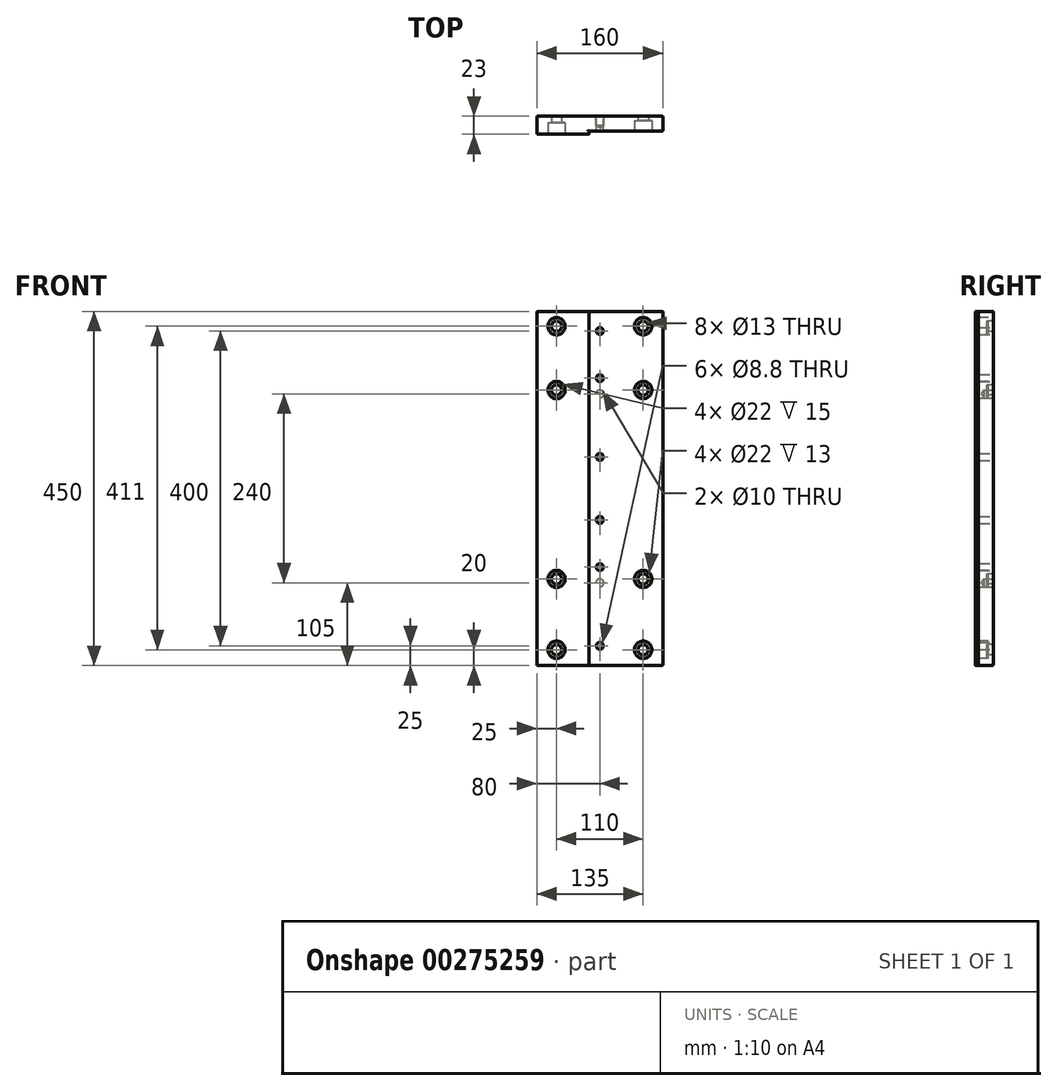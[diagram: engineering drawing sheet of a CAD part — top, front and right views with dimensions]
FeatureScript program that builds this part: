
annotation { "Feature Type Name" : "Feature", "Feature Type Description" : "" }
export const myFeature = defineFeature(function(context is Context, id is Id, definition is map)
    precondition{}
    {
        {
            var Q0;
            Q0=qCreatedBy(makeId("Front.planeOp"),FACE);
            var sketch = newSketch(context, id + "F0", { "sketchPlane" : qUnion([Q0])});
            skLineSegment(sketch, "E0.bottom", {"start": v(80, -225) * mm, "end": v(-80, -225) * mm});
            skLineSegment(sketch, "E0.top", {"start": v(80, 225) * mm, "end": v(-80, 225) * mm});
            skLineSegment(sketch, "E0.left", {"start": v(80, -225) * mm, "end": v(80, 225) * mm});
            skLineSegment(sketch, "E0.right", {"start": v(-80, -225) * mm, "end": v(-80, 225) * mm});
            skPoint(sketch, "E0.middle", {"position": v(0, 0) * mm});
            skLineSegment(sketch, "E1", {"start": v(0, 280.93) * mm, "end": v(0, -292.93) * mm, "construction": true});
            skLineSegment(sketch, "E2", {"start": v(-14, 225) * mm, "end": v(-14, -225) * mm});
            skLineSegment(sketch, "E3", {"start": v(-59.7, 206) * mm, "end": v(63.96, 206) * mm, "construction": true});
            skLineSegment(sketch, "E4", {"start": v(-66.2, -205) * mm, "end": v(62.1, -205) * mm, "construction": true});
            skLineSegment(sketch, "E5", {"start": v(-55, 125) * mm, "end": v(57.45, 125) * mm, "construction": true});
            skLineSegment(sketch, "E6", {"start": v(-48.54, -115) * mm, "end": v(63.03, -115) * mm, "construction": true});
            skPoint(sketch, "E7", {"position": v(0, 200) * mm});
            skPoint(sketch, "E8", {"position": v(0, 140) * mm});
            skPoint(sketch, "E9", {"position": v(0, 120) * mm});
            skPoint(sketch, "E10", {"position": v(0, 40) * mm});
            skPoint(sketch, "E11", {"position": v(0, -40) * mm});
            skPoint(sketch, "E12", {"position": v(0, -100) * mm});
            skPoint(sketch, "E13", {"position": v(0, -120) * mm});
            skPoint(sketch, "E14", {"position": v(0, -200) * mm});
            skPoint(sketch, "E15", {"position": v(-55, 206) * mm});
            skPoint(sketch, "E16", {"position": v(55, 206) * mm});
            skPoint(sketch, "E17", {"position": v(-55, 125) * mm});
            skPoint(sketch, "E18", {"position": v(55, 125) * mm});
            skPoint(sketch, "E19", {"position": v(-55, -115) * mm});
            skPoint(sketch, "E20", {"position": v(55, -115) * mm});
            skPoint(sketch, "E21", {"position": v(-55, -205) * mm});
            skPoint(sketch, "E22", {"position": v(55, -205) * mm});
            skLineSegment(sketch, "E23", {"start": v(-55, -220.48) * mm, "end": v(-55, 225) * mm, "construction": true});
            skLineSegment(sketch, "E24.MirrorCS", {"start": v(55, -220.48) * mm, "end": v(55, 225) * mm, "construction": true});
            skSolve(sketch);
        }
        {
            var Q0;
            {var subQ0=sQuery(id+"F0.wireOp",EDGE,"E0.right");Q0=makeQuery(id+"F0.imprint","IMPRINT",FACE,{"disambiguationData":[TD([[makeQuery(id+"F0.imprint","IMPRINT",EDGE,{"derivedFrom":subQ0}),-1.0]])]});}
            extrude(context, id + "F1", {"entities" : qUnion([Q0]), "depth" : 23 * mm});
        }
        {
            var Q0;
            {var subQ0=sQuery(id+"F0.wireOp",EDGE,"E0.left");Q0=makeQuery(id+"F0.imprint","IMPRINT",FACE,{"disambiguationData":[TD([[makeQuery(id+"F0.imprint","IMPRINT",EDGE,{"derivedFrom":subQ0}),1.0]])]});}
            extrude(context, id + "F2", {"entities" : qUnion([Q0]), "operationType" : NewBodyOperationType.ADD, "depth" : 19 * mm});
        }
        {
            var Q0;
            Q0=sQuery(id+"F0.wireOp",VERTEX,"E13");
            var Q1;
            Q1=sQuery(id+"F0.wireOp",VERTEX,"E9");
            var Q2;
            Q2=makeQuery(id+"F1.opExtrude","SWEPT_BODY",BODY,{"disambiguationData":[OSD([sQuery(id+"F0.wireOp",EDGE,"E0.bottom"),sQuery(id+"F0.wireOp",EDGE,"E0.top"),sQuery(id+"F0.wireOp",EDGE,"E0.right"),sQuery(id+"F0.wireOp",EDGE,"E2")])]});
            hole(context, id + "F3", {"style" : HoleStyle.SIMPLE, "endStyle" : HoleEndStyle.BLIND, "oppositeDirection" : true, "holeDiameter" : 10 * mm, "holeDepth" : 12 * mm, "tappedDepth" : 12 * mm, "tapClearance" : 3, "startFromSketch" : true, "locations" : qUnion([Q0, Q1]), "scope" : qUnion([Q2])});
        }
        {
            var Q0;
            Q0=sQuery(id+"F0.wireOp",VERTEX,"E14");
            var Q1;
            Q1=sQuery(id+"F0.wireOp",VERTEX,"E12");
            var Q2;
            Q2=sQuery(id+"F0.wireOp",VERTEX,"E11");
            var Q3;
            Q3=sQuery(id+"F0.wireOp",VERTEX,"E10");
            var Q4;
            Q4=sQuery(id+"F0.wireOp",VERTEX,"E8");
            var Q5;
            Q5=sQuery(id+"F0.wireOp",VERTEX,"E7");
            var Q6;
            Q6=makeQuery(id+"F1.opExtrude","SWEPT_BODY",BODY,{"disambiguationData":[OSD([sQuery(id+"F0.wireOp",EDGE,"E0.bottom"),sQuery(id+"F0.wireOp",EDGE,"E0.top"),sQuery(id+"F0.wireOp",EDGE,"E0.right"),sQuery(id+"F0.wireOp",EDGE,"E2")])]});
            hole(context, id + "F4", {"style" : HoleStyle.SIMPLE, "endStyle" : HoleEndStyle.BLIND, "oppositeDirection" : true, "standardTappedOrClearance" : lookupTablePath({ "standard" : "ISO", "fit" : "Normal", "size" : "M8", "type" : "Clearance" }), "standardBlindInLast" : lookupTablePath({ "fit" : "Standard", "standard" : "ISO", "size" : "M8", "type" : "Clearance" }), "holeDiameter" : 8.8 * mm, "holeDepth" : 33 * mm, "tappedDepth" : 12 * mm, "tapClearance" : 3, "startFromSketch" : true, "locations" : qUnion([Q0, Q1, Q2, Q3, Q4, Q5]), "scope" : qUnion([Q6])});
        }
        {
            var Q0;
            Q0=makeQuery(id+"F1.opExtrude","CAP_FACE",FACE,{"disambiguationData":[OSD([sQuery(id+"F0.wireOp",EDGE,"E0.bottom"),sQuery(id+"F0.wireOp",EDGE,"E0.top"),sQuery(id+"F0.wireOp",EDGE,"E0.right"),sQuery(id+"F0.wireOp",EDGE,"E2")])],"isStart":false});
            var sketch = newSketch(context, id + "F5", { "sketchPlane" : qUnion([Q0])});
            skPoint(sketch, "E25.0", {"position": v(-55, 206) * mm});
            skPoint(sketch, "E26.0", {"position": v(-55, 125) * mm});
            skPoint(sketch, "E27.0", {"position": v(-55, -115) * mm});
            skPoint(sketch, "E28.0", {"position": v(-55, -205) * mm});
            skSolve(sketch);
        }
        {
            var Q0;
            Q0=sQuery(id+"F5.wireOp",VERTEX,"E25.0");
            var Q1;
            Q1=sQuery(id+"F5.wireOp",VERTEX,"E26.0");
            var Q2;
            Q2=sQuery(id+"F5.wireOp",VERTEX,"E27.0");
            var Q3;
            Q3=sQuery(id+"F5.wireOp",VERTEX,"E28.0");
            var Q4;
            Q4=makeQuery(id+"F1.opExtrude","SWEPT_BODY",BODY,{"disambiguationData":[OSD([sQuery(id+"F0.wireOp",EDGE,"E0.bottom"),sQuery(id+"F0.wireOp",EDGE,"E0.top"),sQuery(id+"F0.wireOp",EDGE,"E0.right"),sQuery(id+"F0.wireOp",EDGE,"E2")])]});
            hole(context, id + "F6", {"style" : HoleStyle.C_BORE, "endStyle" : HoleEndStyle.BLIND, "holeDiameter" : 13 * mm, "cBoreDiameter" : 22 * mm, "cBoreDepth" : 15 * mm, "holeDepth" : 30 * mm, "tappedDepth" : 12 * mm, "tapClearance" : 3, "startFromSketch" : true, "locations" : qUnion([Q0, Q1, Q2, Q3]), "scope" : qUnion([Q4])});
        }
        {
            var Q0;
            Q0=makeQuery(id+"F2.opExtrude","CAP_FACE",FACE,{"disambiguationData":[OSD([sQuery(id+"F0.wireOp",EDGE,"E0.bottom"),sQuery(id+"F0.wireOp",EDGE,"E0.top"),sQuery(id+"F0.wireOp",EDGE,"E0.left"),sQuery(id+"F0.wireOp",EDGE,"E2")])],"isStart":false});
            var sketch = newSketch(context, id + "F7", { "sketchPlane" : qUnion([Q0])});
            skPoint(sketch, "E29.0", {"position": v(55, 206) * mm});
            skPoint(sketch, "E30.0", {"position": v(55, 125) * mm});
            skPoint(sketch, "E31.0", {"position": v(55, -115) * mm});
            skPoint(sketch, "E32.0", {"position": v(55, -205) * mm});
            skSolve(sketch);
        }
        {
            var Q0;
            Q0=sQuery(id+"F7.wireOp",VERTEX,"E29.0");
            var Q1;
            Q1=sQuery(id+"F7.wireOp",VERTEX,"E30.0");
            var Q2;
            Q2=sQuery(id+"F7.wireOp",VERTEX,"E31.0");
            var Q3;
            Q3=sQuery(id+"F7.wireOp",VERTEX,"E32.0");
            var Q4;
            Q4=makeQuery(id+"F1.opExtrude","SWEPT_BODY",BODY,{"disambiguationData":[OSD([sQuery(id+"F0.wireOp",EDGE,"E0.bottom"),sQuery(id+"F0.wireOp",EDGE,"E0.top"),sQuery(id+"F0.wireOp",EDGE,"E0.right"),sQuery(id+"F0.wireOp",EDGE,"E2")])]});
            hole(context, id + "F8", {"style" : HoleStyle.C_BORE, "endStyle" : HoleEndStyle.BLIND, "holeDiameter" : 13 * mm, "cBoreDiameter" : 22 * mm, "cBoreDepth" : 13 * mm, "holeDepth" : 30 * mm, "tappedDepth" : 12 * mm, "tapClearance" : 3, "startFromSketch" : true, "locations" : qUnion([Q0, Q1, Q2, Q3]), "scope" : qUnion([Q4])});
        }
        {
            var Q0;
            Q0=makeQuery(id+"F1.opExtrude","SWEPT_FACE",FACE,{"disambiguationData":[OSD([sQuery(id+"F0.wireOp",EDGE,"E0.right")])]});
            var Q1;
            {var subQ0=sQuery(id+"F0.wireOp",EDGE,"E0.top");Q1=makeQuery(id+"F2.boolean.opBoolean","MERGE",FACE,{"derivedFrom":[makeQuery(id+"F1.opExtrude","SWEPT_FACE",FACE,{"disambiguationData":[OSD([subQ0])]}),makeQuery(id+"F2.opExtrude","SWEPT_FACE",FACE,{"disambiguationData":[OSD([subQ0])]})]});}
            var Q2;
            Q2=makeQuery(id+"F2.opExtrude","SWEPT_FACE",FACE,{"disambiguationData":[OSD([sQuery(id+"F0.wireOp",EDGE,"E0.left")])]});
            var Q3;
            {var subQ0=sQuery(id+"F0.wireOp",EDGE,"E0.bottom");Q3=makeQuery(id+"F2.boolean.opBoolean","MERGE",FACE,{"derivedFrom":[makeQuery(id+"F1.opExtrude","SWEPT_FACE",FACE,{"disambiguationData":[OSD([subQ0])]}),makeQuery(id+"F2.opExtrude","SWEPT_FACE",FACE,{"disambiguationData":[OSD([subQ0])]})]});}
            fillet(context, id + "F9", {"entities" : qUnion([Q0, Q1, Q2, Q3]), "radius" : 1 * mm, "tangentPropagation" : true, "allowEdgeOverflow" : false});
        }
    });
